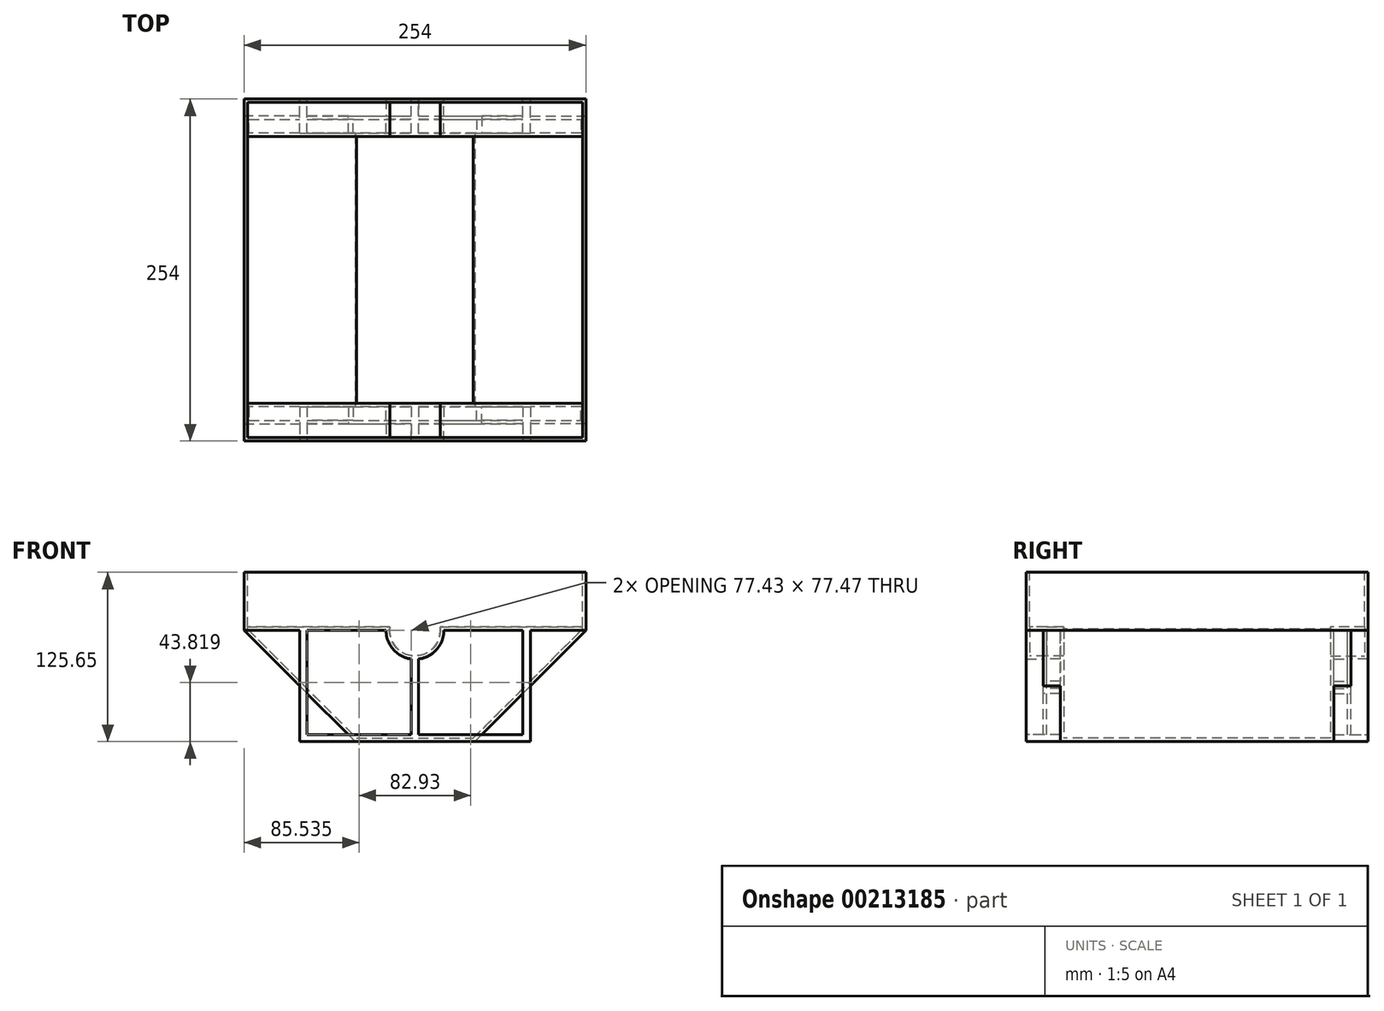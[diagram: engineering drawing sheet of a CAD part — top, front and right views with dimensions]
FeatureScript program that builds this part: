
annotation { "Feature Type Name" : "Feature", "Feature Type Description" : "" }
export const myFeature = defineFeature(function(context is Context, id is Id, definition is map)
    precondition{}
    {
        {
            var Q0;
            Q0=qCreatedBy(makeId("Top.planeOp"),FACE);
            var sketch = newSketch(context, id + "F0", { "sketchPlane" : qUnion([Q0])});
            skLineSegment(sketch, "E0.bottom", {"start": v(-127, 127) * mm, "end": v(127, 127) * mm});
            skLineSegment(sketch, "E0.top", {"start": v(-127, -127) * mm, "end": v(127, -127) * mm});
            skLineSegment(sketch, "E0.left", {"start": v(-127, 127) * mm, "end": v(-127, -127) * mm});
            skLineSegment(sketch, "E0.right", {"start": v(127, 127) * mm, "end": v(127, -127) * mm});
            skSolve(sketch);
        }
        {
            var Q0;
            Q0=makeQuery(id+"F0.imprint","IMPRINT",FACE,{"disambiguationData":[TD([[makeQuery(id+"F0.imprint","IMPRINT",EDGE,{"derivedFrom":sQuery(id+"F0.wireOp",EDGE,"E0.bottom")}),-1.0]])]});
            extrude(context, id + "F1", {"entities" : qUnion([Q0]), "oppositeDirection" : true, "depth" : 127 * mm});
        }
        {
            var Q0;
            Q0=qCreatedBy(makeId("Front.planeOp"),FACE);
            var sketch = newSketch(context, id + "F2", { "sketchPlane" : qUnion([Q0])});
            skLineSegment(sketch, "E1", {"start": v(-127, -43.1) * mm, "end": v(-44.45, -125.65) * mm});
            skLineSegment(sketch, "E2", {"start": v(-44.45, -125.65) * mm, "end": v(44.45, -125.65) * mm});
            skLineSegment(sketch, "E3", {"start": v(44.45, -125.65) * mm, "end": v(127, -43.1) * mm});
            skLineSegment(sketch, "E4", {"start": v(127, -43.1) * mm, "end": v(160.2, -43.1) * mm});
            skLineSegment(sketch, "E5", {"start": v(160.2, -43.1) * mm, "end": v(160.2, -156.35) * mm});
            skLineSegment(sketch, "E6", {"start": v(160.2, -156.35) * mm, "end": v(-141.22, -156.35) * mm});
            skLineSegment(sketch, "E7", {"start": v(-141.22, -156.35) * mm, "end": v(-141.22, -43.1) * mm});
            skLineSegment(sketch, "E8", {"start": v(-141.22, -43.1) * mm, "end": v(-127, -43.1) * mm});
            skSolve(sketch);
        }
        {
            var Q0;
            Q0=makeQuery(id+"F2.imprint","IMPRINT",FACE,{"disambiguationData":[TD([[makeQuery(id+"F2.imprint","IMPRINT",EDGE,{"derivedFrom":sQuery(id+"F2.wireOp",EDGE,"E1")}),-1.0]])]});
            extrude(context, id + "F3", {"entities" : qUnion([Q0]), "operationType" : NewBodyOperationType.REMOVE, "endBound" : BoundingType.SYMMETRIC, "oppositeDirection" : true, "depth" : 357.63 * mm});
        }
        {
            var Q0;
            Q0=makeQuery(id+"F1.opExtrude","SWEPT_FACE",FACE,{"disambiguationData":[OSD([sQuery(id+"F0.wireOp",EDGE,"E0.top")])]});
            var sketch = newSketch(context, id + "F4", { "sketchPlane" : qUnion([Q0])});
            skLineSegment(sketch, "E9.bottom", {"start": v(-153.35, -43.1) * mm, "end": v(-21.44, -43.1) * mm});
            skLineSegment(sketch, "E9.top", {"start": v(-153.35, -154.57) * mm, "end": v(138.01, -154.57) * mm});
            skLineSegment(sketch, "E9.left", {"start": v(-153.35, -43.1) * mm, "end": v(-153.35, -154.57) * mm});
            skLineSegment(sketch, "E9.right", {"start": v(138.01, -43.1) * mm, "end": v(138.01, -154.57) * mm});
            skArc(sketch, "E10", {"start": v(-21.44, -43.1) * mm, "mid": v(0, -64.53) * mm, "end": v(21.44, -43.1) * mm});
            skLineSegment(sketch, "E11.trimOffspring", {"start": v(21.44, -43.1) * mm, "end": v(138.01, -43.1) * mm});
            skSolve(sketch);
        }
        {
            var Q0;
            Q0=makeQuery(id+"F4.imprint","IMPRINT",FACE,{"disambiguationData":[TD([[makeQuery(id+"F4.imprint","IMPRINT",EDGE,{"derivedFrom":sQuery(id+"F4.wireOp",EDGE,"E9.top")}),1.0]])]});
            var Q1;
            {var subQ1=sQuery(id+"F0.wireOp",EDGE,"E0.top");var subQ2=makeQuery(id+"F1.opExtrude","SWEPT_FACE",FACE,{"disambiguationData":[OSD([subQ1])]});var subQ3=makeQuery(id+"F3.boolean.opBoolean","INTERSECT",EDGE,{"derivedFrom":[subQ2,makeQuery(id+"F3.opExtrude","SWEPT_FACE",FACE,{"disambiguationData":[OSD([sQuery(id+"F2.wireOp",EDGE,"E1")])]})]});Q1=makeQuery(id+"F4.imprint","IMPRINT",FACE,{"disambiguationData":[TD([[makeQuery(id+"F4.imprint","IMPRINT",EDGE,{"derivedFrom":subQ3}),1.0]])]});}
            extrude(context, id + "F5", {"entities" : qUnion([Q0, Q1]), "operationType" : NewBodyOperationType.REMOVE, "oppositeDirection" : true, "depth" : 12.7 * mm});
        }
        {
            var Q0;
            Q0=makeQuery(id+"F1.opExtrude","SWEPT_FACE",FACE,{"disambiguationData":[OSD([sQuery(id+"F0.wireOp",EDGE,"E0.bottom")])]});
            var sketch = newSketch(context, id + "F6", { "sketchPlane" : qUnion([Q0])});
            skLineSegment(sketch, "E12.bottom", {"start": v(-169.86, -43.1) * mm, "end": v(-21.44, -43.1) * mm});
            skLineSegment(sketch, "E12.top", {"start": v(-169.86, -186.42) * mm, "end": v(248.3, -186.42) * mm});
            skLineSegment(sketch, "E12.left", {"start": v(-169.86, -43.1) * mm, "end": v(-169.86, -186.42) * mm});
            skLineSegment(sketch, "E12.right", {"start": v(248.3, -43.1) * mm, "end": v(248.3, -186.42) * mm});
            skArc(sketch, "E13", {"start": v(-21.44, -43.1) * mm, "mid": v(0, -64.54) * mm, "end": v(21.44, -43.1) * mm});
            skLineSegment(sketch, "E14.trimOffspring", {"start": v(21.44, -43.1) * mm, "end": v(248.3, -43.1) * mm});
            skSolve(sketch);
        }
        {
            var Q0;
            Q0=qSketchRegion(id+"F6",true);
            extrude(context, id + "F7", {"entities" : qUnion([Q0]), "operationType" : NewBodyOperationType.REMOVE, "oppositeDirection" : true, "depth" : 25.4 * mm});
        }
        {
            var Q0;
            Q0=makeQuery(id+"F1.opExtrude","CAP_FACE",FACE,{"disambiguationData":[OSD([sQuery(id+"F0.wireOp",EDGE,"E0.bottom"),sQuery(id+"F0.wireOp",EDGE,"E0.top"),sQuery(id+"F0.wireOp",EDGE,"E0.left"),sQuery(id+"F0.wireOp",EDGE,"E0.right")])],"isStart":true});
            shell(context, id + "F8", {"entities" : qUnion([Q0]), "thickness" : 2.54 * mm});
        }
        {
            var Q0;
            Q0=makeQuery(id+"F1.opExtrude","SWEPT_FACE",FACE,{"disambiguationData":[OSD([sQuery(id+"F0.wireOp",EDGE,"E0.bottom")])]});
            var sketch = newSketch(context, id + "F9", { "sketchPlane" : qUnion([Q0])});
            skLineSegment(sketch, "E15.bottom", {"start": v(-85.68, -43.1) * mm, "end": v(-80.18, -43.1) * mm});
            skLineSegment(sketch, "E15.top", {"start": v(-85.68, -125.65) * mm, "end": v(-80.18, -125.65) * mm});
            skLineSegment(sketch, "E15.left", {"start": v(-85.68, -43.1) * mm, "end": v(-85.68, -125.65) * mm});
            skLineSegment(sketch, "E15.right", {"start": v(-80.18, -43.1) * mm, "end": v(-80.18, -120.57) * mm});
            skLineSegment(sketch, "E16.MirrorCS", {"start": v(85.68, -125.65) * mm, "end": v(80.18, -125.65) * mm});
            skLineSegment(sketch, "E17.MirrorCS", {"start": v(85.68, -43.1) * mm, "end": v(80.18, -43.1) * mm});
            skLineSegment(sketch, "E18.MirrorCS", {"start": v(85.68, -43.1) * mm, "end": v(85.68, -125.65) * mm});
            skLineSegment(sketch, "E19.MirrorCS", {"start": v(80.18, -43.1) * mm, "end": v(80.18, -120.57) * mm});
            skLineSegment(sketch, "E20.bottom", {"start": v(-80.18, -120.57) * mm, "end": v(-2.75, -120.57) * mm});
            skLineSegment(sketch, "E20.top", {"start": v(-80.18, -125.65) * mm, "end": v(80.18, -125.65) * mm});
            skLineSegment(sketch, "E21.bottom", {"start": v(-2.75, -55.03) * mm, "end": v(2.75, -55.03) * mm});
            skLineSegment(sketch, "E21.left", {"start": v(-2.75, -55.03) * mm, "end": v(-2.75, -120.57) * mm});
            skLineSegment(sketch, "E21.right", {"start": v(2.75, -55.03) * mm, "end": v(2.75, -120.57) * mm});
            skLineSegment(sketch, "E22.trimOffspring", {"start": v(2.75, -120.57) * mm, "end": v(80.18, -120.57) * mm});
            skSolve(sketch);
        }
        {
            var Q0;
            Q0=makeQuery(id+"F9.imprint","IMPRINT",FACE,{"disambiguationData":[TD([[makeQuery(id+"F9.imprint","IMPRINT",EDGE,{"derivedFrom":sQuery(id+"F9.wireOp",EDGE,"E15.bottom")}),-1.0]])]});
            var Q1;
            Q1=makeQuery(id+"F7.boolean.opBoolean","COPY",FACE,{"derivedFrom":makeQuery(id+"F7.opExtrude","CAP_FACE",FACE,{"disambiguationData":[OSD([sQuery(id+"F6.wireOp",EDGE,"E12.bottom"),sQuery(id+"F6.wireOp",EDGE,"E12.top"),sQuery(id+"F6.wireOp",EDGE,"E12.left"),sQuery(id+"F6.wireOp",EDGE,"E12.right"),sQuery(id+"F6.wireOp",EDGE,"E13"),sQuery(id+"F6.wireOp",EDGE,"E14.trimOffspring")])],"isStart":false})});
            extrude(context, id + "F10", {"entities" : qUnion([Q0]), "operationType" : NewBodyOperationType.ADD, "endBound" : BoundingType.UP_TO_SURFACE, "oppositeDirection" : true, "endBoundEntityFace" : qUnion([Q1]), "depth" : 25.4 * mm});
        }
        {
            var Q0;
            Q0=makeQuery(id+"F1.opExtrude","SWEPT_BODY",BODY,{"disambiguationData":[OSD([sQuery(id+"F0.wireOp",EDGE,"E0.bottom"),sQuery(id+"F0.wireOp",EDGE,"E0.top"),sQuery(id+"F0.wireOp",EDGE,"E0.left"),sQuery(id+"F0.wireOp",EDGE,"E0.right")])]});
            var Q1;
            Q1=qCreatedBy(makeId("Front.planeOp"),FACE);
            mirror(context, id + "F11", {"operationType" : NewBodyOperationType.ADD, "entities" : qUnion([Q0]), "mirrorPlane" : qUnion([Q1])});
        }
    });
